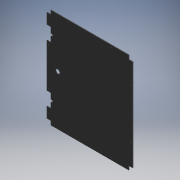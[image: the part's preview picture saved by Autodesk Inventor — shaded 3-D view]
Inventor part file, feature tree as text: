
AUTODESK INVENTOR PART (.ipt)
format: ipt  version: 2017.3 (Build 213256000, 256)  size: 207,872 bytes
history: native  units: mm
features: extrude x4, sketch x4, mirror x1, fillet x1
ambient origin geometry x8: Origin, YZ Plane, XZ Plane, XY Plane, X Axis, Y Axis, Z Axis, Center Point
bodies: Body1 (feature_tree)
feature tree (10):
  extrude  "Extrusion2"  Depth=440.0mm
  extrude  "Extrusion3"  Depth=3.0mm TaperAngle=0.0deg
  extrude  "Extrusion4"  Depth=10.0mm
  extrude  "Extrusion5"  Depth=20.0mm
  mirror  "Mirror1"
  fillet  "Fillet1"  Radius=4.2mm
  sketch  "Sketch1"  dims[d0=510.0mm d1=440.0mm]
  sketch  "Sketch2"  dims[d2=20.0mm d5=3.0mm d6=0.0mm]
  sketch  "Sketch3"  dims[d7=10.0mm d8=10.0mm]
  sketch  "Sketch4"  dims[d9=117.5mm d10=100.0mm d11=4.2mm d12=3.0mm d13=0.0mm d14=40.0mm d15=22.0mm d16=31.0mm d17=3.4mm d18=10.0mm d19=0.0mm d21=70.5mm d22=12.5mm d23=8.5mm d24=10.0mm d25=0.0mm d26=1.0mm d27=147.0mm d28=20.0mm d29=88.5mm]
